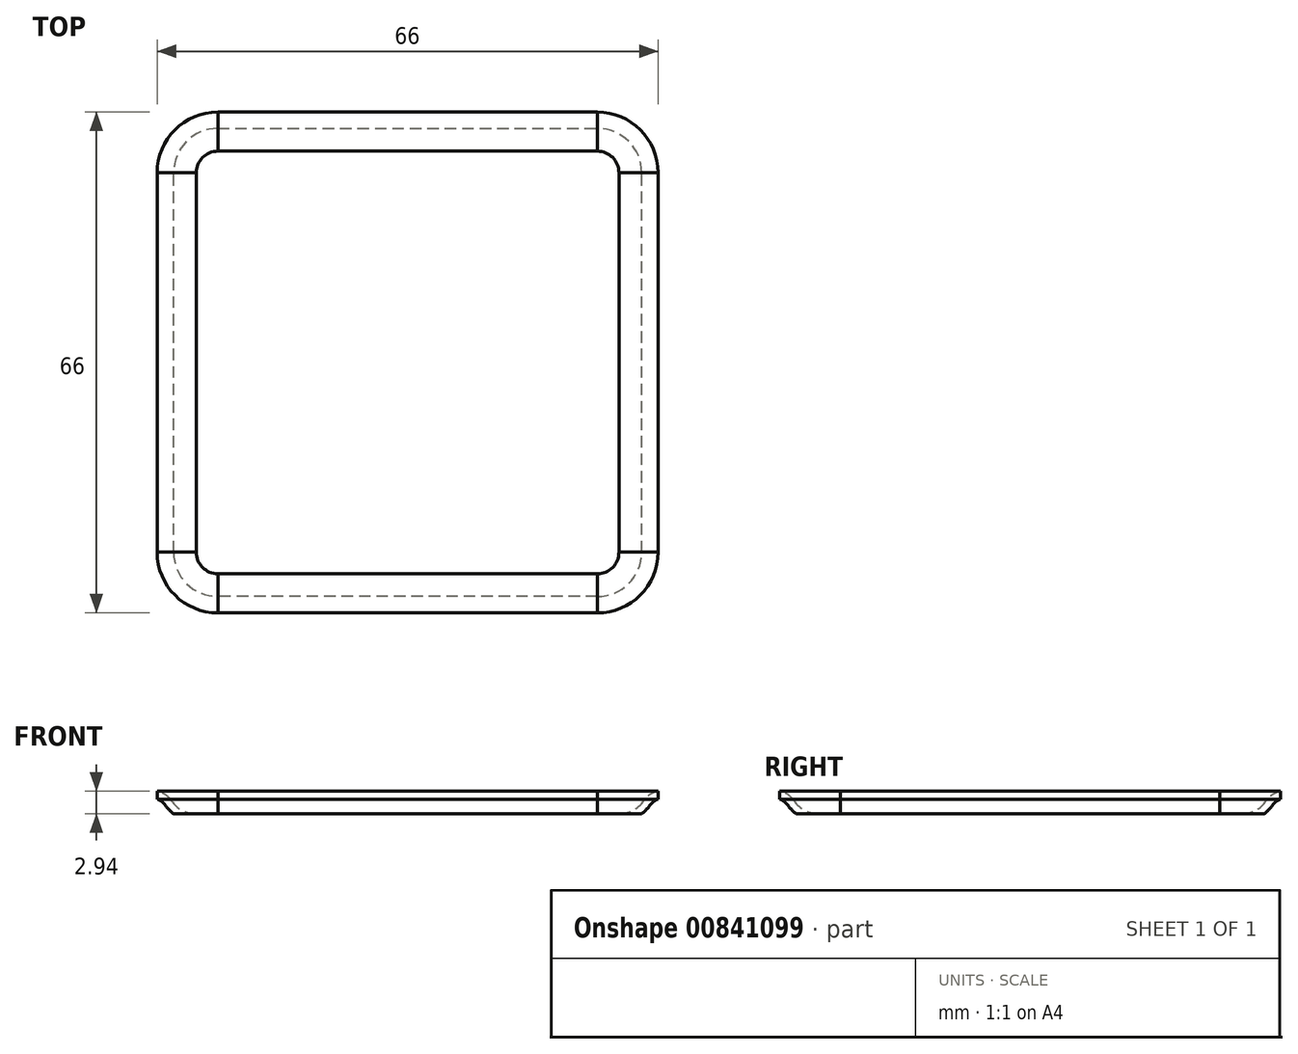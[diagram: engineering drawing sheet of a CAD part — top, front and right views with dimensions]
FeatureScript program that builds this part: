
annotation { "Feature Type Name" : "Feature", "Feature Type Description" : "" }
export const myFeature = defineFeature(function(context is Context, id is Id, definition is map)
    precondition{}
    {
        {
            var Q0;
            Q0=qCreatedBy(makeId("Front.planeOp"),FACE);
            var sketch = newSketch(context, id + "F0", { "sketchPlane" : qUnion([Q0])});
            skPoint(sketch, "E0", {"position": v(-33, 4.94) * mm});
            skPoint(sketch, "E1", {"position": v(-31.12, 3.71) * mm});
            skPoint(sketch, "E2", {"position": v(-27.84, 2) * mm});
            skArc(sketch, "E3", {"start": v(-31.12, 3.71) * mm, "mid": v(-31.94, 4.51) * mm, "end": v(-33, 4.94) * mm});
            skArc(sketch, "E4", {"start": v(-31.12, 3.71) * mm, "mid": v(-29.69, 2.45) * mm, "end": v(-27.84, 2) * mm});
            skArc(sketch, "E5.0", {"start": v(-31.94, 3.14) * mm, "mid": v(-31.44, 2.53) * mm, "end": v(-30.84, 2) * mm});
            skArc(sketch, "E5.1", {"start": v(-31.94, 3.14) * mm, "mid": v(-32.4, 3.62) * mm, "end": v(-33, 3.91) * mm});
            skLineSegment(sketch, "E6", {"start": v(-33, 3.91) * mm, "end": v(-33, 4.94) * mm});
            skLineSegment(sketch, "E7", {"start": v(-30.84, 2) * mm, "end": v(-27.84, 2) * mm});
            skSolve(sketch);
        }
        {
            var Q0;
            Q0 = qSketchRegion(id + "F0", true);
            var Q1;
            Q1 = qConstructionFilter(qBodyType(qCreatedBy(id + "F0" ,EDGE), BodyType.WIRE), ConstructionObject.NO);
            extrude(context, id + "F1", {"entities" : qUnion([Q0]), "surfaceEntities" : qUnion([Q1]), "endBound" : BoundingType.SYMMETRIC, "depth" : 50 * mm, "offsetDistance" : 25 * mm});
        }
        {
            var Q0;
            Q0=makeQuery(id+"F1.opExtrude","SWEPT_BODY",BODY,{"disambiguationData":[OSD([sQuery(id+"F0.wireOp",EDGE,"E5.1")])]});
            var Q1;
            Q1=qCreatedBy(makeId("Right.planeOp"),FACE);
            mirror(context, id + "F2", {"entities" : qUnion([Q0]), "mirrorPlane" : qUnion([Q1])});
        }
        {
            var Q0;
            Q0=qCreatedBy(makeId("Right.planeOp"),FACE);
            var sketch = newSketch(context, id + "F3", { "sketchPlane" : qUnion([Q0])});
            skLineSegment(sketch, "E8", {"start": v(0, 0) * mm, "end": v(0, 16.96) * mm});
            skSolve(sketch);
        }
        {
            var Q0;
            Q0=makeQuery(id+"F1.opExtrude","SWEPT_BODY",BODY,{"disambiguationData":[OSD([sQuery(id+"F0.wireOp",EDGE,"E5.1")])]});
            var Q1;
            Q1=makeQuery(id+"F2.opPattern","COPY",BODY,{"derivedFrom":makeQuery(id+"F1.opExtrude","SWEPT_BODY",BODY,{"disambiguationData":[OSD([sQuery(id+"F0.wireOp",EDGE,"E5.1")])]}),"instanceName":"1"});
            var Q2;
            Q2=sQuery(id+"F3.wireOp",EDGE,"E8");
            circularPattern(context, id + "F4", {"entities" : qUnion([Q0, Q1]), "axis" : qUnion([Q2]), "angle" : 360 * degree, "instanceCount" : 4, "equalSpace" : true});
        }
        {
            var Q0;
            Q0=makeQuery(id+"F4.opPattern","COPY",FACE,{"derivedFrom":makeQuery(id+"F1.opExtrude","CAP_FACE",FACE,{"disambiguationData":[OSD([sQuery(id+"F0.wireOp",EDGE,"E3"),sQuery(id+"F0.wireOp",EDGE,"E4"),sQuery(id+"F0.wireOp",EDGE,"E5.0"),sQuery(id+"F0.wireOp",EDGE,"E5.1"),sQuery(id+"F0.wireOp",EDGE,"E6"),sQuery(id+"F0.wireOp",EDGE,"E7")])],"isStart":false}),"instanceName":"1"});
            var sketch = newSketch(context, id + "F5", { "sketchPlane" : qUnion([Q0])});
            skPoint(sketch, "E9", {"position": v(-25, 2) * mm});
            skLineSegment(sketch, "E10", {"start": v(-25, 2) * mm, "end": v(-25, -2.36) * mm});
            skSolve(sketch);
        }
        {
            var Q0;
            Q0=makeQuery(id+"F4.opPattern","COPY",FACE,{"derivedFrom":makeQuery(id+"F1.opExtrude","CAP_FACE",FACE,{"disambiguationData":[OSD([sQuery(id+"F0.wireOp",EDGE,"E3"),sQuery(id+"F0.wireOp",EDGE,"E4"),sQuery(id+"F0.wireOp",EDGE,"E5.0"),sQuery(id+"F0.wireOp",EDGE,"E5.1"),sQuery(id+"F0.wireOp",EDGE,"E6"),sQuery(id+"F0.wireOp",EDGE,"E7")])],"isStart":false}),"instanceName":"1"});
            var Q1;
            Q1=sQuery(id+"F5.wireOp",EDGE,"E10");
            revolve(context, id + "F6", {"surfaceOperationType" : NewSurfaceOperationType.NEW, "entities" : qUnion([Q0]), "axis" : qUnion([Q1]), "revolveType" : RevolveType.ONE_DIRECTION, "oppositeDirection" : true, "angle" : 90 * degree});
        }
        {
            var Q0;
            Q0=qCreatedBy(makeId("Right.planeOp"),FACE);
            var sketch = newSketch(context, id + "F7", { "sketchPlane" : qUnion([Q0])});
            skLineSegment(sketch, "E11", {"start": v(0, 0) * mm, "end": v(0, 14.77) * mm});
            skSolve(sketch);
        }
        {
            var Q0;
            Q0=makeQuery(id+"F6.opRevolve","SWEPT_BODY",BODY,{"disambiguationData":[OSD([sQuery(id+"F0.wireOp",EDGE,"E3"),sQuery(id+"F0.wireOp",EDGE,"E4"),sQuery(id+"F0.wireOp",EDGE,"E5.0"),sQuery(id+"F0.wireOp",EDGE,"E5.1"),sQuery(id+"F0.wireOp",EDGE,"E6"),sQuery(id+"F0.wireOp",EDGE,"E7")])]});
            var Q1;
            Q1=sQuery(id+"F7.wireOp",EDGE,"E11");
            circularPattern(context, id + "F8", {"entities" : qUnion([Q0]), "axis" : qUnion([Q1]), "angle" : 360 * degree, "instanceCount" : 4, "equalSpace" : true});
        }
    });
